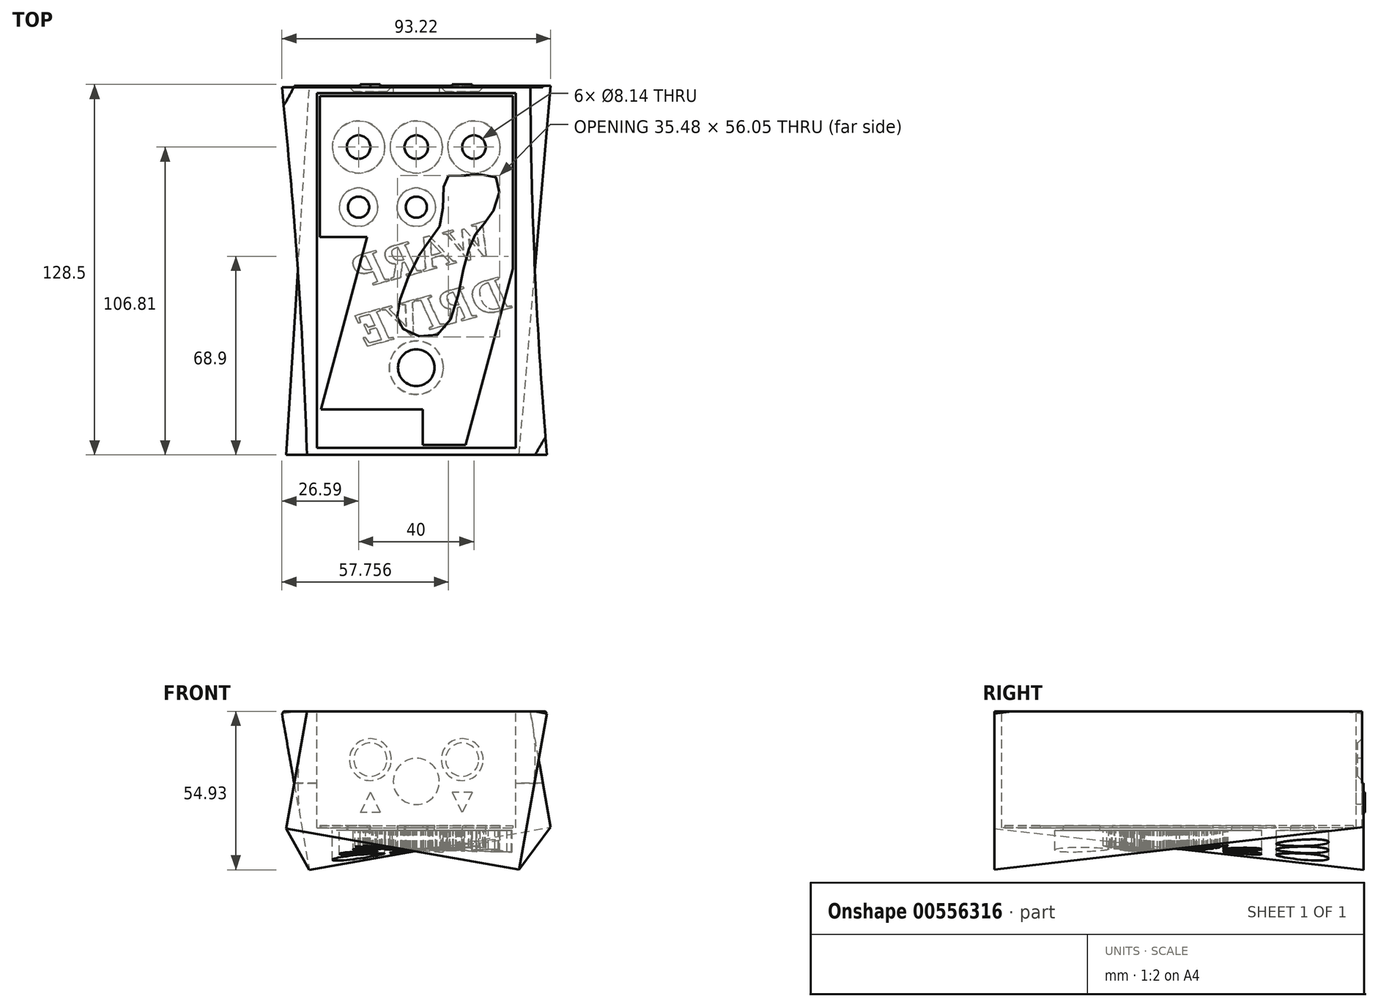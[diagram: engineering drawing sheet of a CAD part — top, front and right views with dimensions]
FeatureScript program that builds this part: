
annotation { "Feature Type Name" : "Feature", "Feature Type Description" : "" }
export const myFeature = defineFeature(function(context is Context, id is Id, definition is map)
    precondition{}
    {
        {
            var Q0;
            Q0=qCreatedBy(makeId("Top.planeOp"),FACE);
            var sketch = newSketch(context, id + "F0", { "sketchPlane" : qUnion([Q0])});
            skLineSegment(sketch, "E0.bottom", {"start": v(-36.5, 64) * mm, "end": v(36.5, 64) * mm});
            skLineSegment(sketch, "E0.top", {"start": v(-36.5, -64) * mm, "end": v(36.5, -64) * mm});
            skLineSegment(sketch, "E0.left", {"start": v(-36.5, 64) * mm, "end": v(-36.5, -64) * mm});
            skLineSegment(sketch, "E0.right", {"start": v(36.5, 64) * mm, "end": v(36.5, -64) * mm});
            skSolve(sketch);
        }
        {
            var Q0;
            Q0=makeQuery(id+"F0.imprint","IMPRINT",FACE,{"disambiguationData":[TD([[makeQuery(id+"F0.imprint","IMPRINT",EDGE,{"derivedFrom":sQuery(id+"F0.wireOp",EDGE,"E0.bottom")}),-1.0]])]});
            extrude(context, id + "F1", {"entities" : qUnion([Q0]), "depth" : 41.2 * mm, "offsetDistance" : 25 * mm});
        }
        {
            var Q0;
            Q0=makeQuery(id+"F1.opExtrude","SWEPT_FACE",FACE,{"disambiguationData":[OSD([sQuery(id+"F0.wireOp",EDGE,"E0.top")])]});
            var sketch = newSketch(context, id + "F2", { "sketchPlane" : qUnion([Q0])});
            skLineSegment(sketch, "E1.0", {"start": v(-36.5, 41.2) * mm, "end": v(-36.5, 0) * mm, "construction": true});
            skLineSegment(sketch, "E2", {"start": v(-36.5, 20.6) * mm, "end": v(36.5, 20.6) * mm, "construction": true});
            skLineSegment(sketch, "E3.bottom", {"start": v(-35.52, 54.74) * mm, "end": v(45.24, 40.5) * mm});
            skLineSegment(sketch, "E3.top", {"start": v(-45.07, 0.57) * mm, "end": v(35.68, -13.67) * mm});
            skLineSegment(sketch, "E3.left", {"start": v(-35.52, 54.74) * mm, "end": v(-45.07, 0.57) * mm});
            skLineSegment(sketch, "E3.right", {"start": v(45.24, 40.5) * mm, "end": v(35.68, -13.67) * mm});
            skPoint(sketch, "E3.middle", {"position": v(0, 20.6) * mm});
            skSolve(sketch);
        }
        {
            var Q0;
            Q0=makeQuery(id+"F1.opExtrude","SWEPT_FACE",FACE,{"disambiguationData":[OSD([sQuery(id+"F0.wireOp",EDGE,"E0.bottom")])]});
            var sketch = newSketch(context, id + "F3", { "sketchPlane" : qUnion([Q0])});
            skLineSegment(sketch, "E4.bottom", {"start": v(46.63, 40.44) * mm, "end": v(-37.08, 55.2) * mm});
            skLineSegment(sketch, "E4.top", {"start": v(37.08, -13.73) * mm, "end": v(-46.63, 1.03) * mm});
            skLineSegment(sketch, "E4.left", {"start": v(46.63, 40.44) * mm, "end": v(37.08, -13.73) * mm});
            skLineSegment(sketch, "E4.right", {"start": v(-37.08, 55.2) * mm, "end": v(-46.63, 1.03) * mm});
            skPoint(sketch, "E4.middle", {"position": v(0, 20.73) * mm});
            skSolve(sketch);
        }
        {
            var Q1;
            Q1 = qSketchRegion(id + "F2", true);
            var Q2;
            Q2 = qSketchRegion(id + "F3", true);
            var Q3;
            Q3=sQuery(id+"F2.wireOp",VERTEX,"E3.bottom.end");
            var Q4;
            Q4=sQuery(id+"F3.wireOp",VERTEX,"E4.bottom.end");
            loft(context, id + "F4", {"operationType" : NewBodyOperationType.ADD, "sheetProfilesArray" : [{ "sheetProfileEntities" : qUnion([Q1]) }, { "sheetProfileEntities" : qUnion([Q2]) }], "matchConnections" : true, "connections" : [{ "connectionEntities" : qUnion([Q3, Q4]), "connectionEdgeQueries" : qUnion([]), "connectionEdgeParameters" : [] }]});
        }
        {
            var Q0;
            Q0=qCreatedBy(makeId("Top.planeOp"),FACE);
            cPlane(context, id + "F5", {"entities" : qUnion([Q0]), "cplaneType" : CPlaneType.OFFSET, "offset" : 41.2 * mm, "width" : 150 * mm, "height" : 150 * mm});
        }
        {
            var Q0;
            Q0=qCreatedBy(id+"F5.planeOp",FACE);
            var sketch = newSketch(context, id + "F6", { "sketchPlane" : qUnion([Q0])});
            skLineSegment(sketch, "E5.bottom", {"start": v(-34.5, 61.5) * mm, "end": v(34.5, 61.5) * mm});
            skLineSegment(sketch, "E5.top", {"start": v(-34.5, -61.5) * mm, "end": v(34.5, -61.5) * mm});
            skLineSegment(sketch, "E5.left", {"start": v(-34.5, 61.5) * mm, "end": v(-34.5, -61.5) * mm});
            skLineSegment(sketch, "E5.right", {"start": v(34.5, 61.5) * mm, "end": v(34.5, -61.5) * mm});
            skSolve(sketch);
        }
        {
            var Q0;
            Q0=makeQuery(id+"F6.imprint","IMPRINT",FACE,{"disambiguationData":[TD([[makeQuery(id+"F6.imprint","IMPRINT",EDGE,{"derivedFrom":sQuery(id+"F6.wireOp",EDGE,"E5.bottom")}),-1.0]])]});
            extrude(context, id + "F7", {"entities" : qUnion([Q0]), "operationType" : NewBodyOperationType.REMOVE, "oppositeDirection" : true, "depth" : 40.4 * mm, "offsetDistance" : 25 * mm, "hasSecondDirection" : true, "secondDirectionOppositeDirection" : false, "secondDirectionDepth" : 25 * mm});
        }
        {
            var Q0;
            Q0=makeQuery(id+"F7.boolean.opBoolean","COPY",FACE,{"derivedFrom":makeQuery(id+"F7.opExtrude","CAP_FACE",FACE,{"disambiguationData":[OSD([sQuery(id+"F6.wireOp",EDGE,"E5.bottom"),sQuery(id+"F6.wireOp",EDGE,"E5.top"),sQuery(id+"F6.wireOp",EDGE,"E5.left"),sQuery(id+"F6.wireOp",EDGE,"E5.right")])],"isStart":false})});
            var sketch = newSketch(context, id + "F8", { "sketchPlane" : qUnion([Q0])});
            skCircle(sketch, "E6", {"center": v(-20, 42.8) * mm, "radius": 4.07 * mm});
            skCircle(sketch, "E7", {"center": v(0, 42.8) * mm, "radius": 4.07 * mm});
            skCircle(sketch, "E8", {"center": v(20, 42.8) * mm, "radius": 4.07 * mm});
            skCircle(sketch, "E9", {"center": v(0, -33.73) * mm, "radius": 6.35 * mm});
            skLineSegment(sketch, "E10", {"start": v(20, 42.8) * mm, "end": v(0, 42.8) * mm, "construction": true});
            skCircle(sketch, "E11", {"center": v(0, 21.96) * mm, "radius": 3.67 * mm});
            skCircle(sketch, "E12", {"center": v(-20, 21.96) * mm, "radius": 3.67 * mm});
            skSolve(sketch);
        }
        {
            var Q0;
            Q0=qSketchRegion(id+"F8",true);
            extrude(context, id + "F9", {"entities" : qUnion([Q0]), "operationType" : NewBodyOperationType.REMOVE, "oppositeDirection" : true, "depth" : 25 * mm, "offsetDistance" : 25 * mm});
        }
        {
            var Q0;
            Q0=makeQuery(id+"F7.boolean.opBoolean","COPY",FACE,{"derivedFrom":makeQuery(id+"F7.opExtrude","SWEPT_FACE",FACE,{"disambiguationData":[OSD([sQuery(id+"F6.wireOp",EDGE,"E5.bottom")])]})});
            cPlane(context, id + "F10", {"entities" : qUnion([Q0]), "cplaneType" : CPlaneType.OFFSET, "offset" : 2 * mm, "oppositeDirection" : true, "width" : 150 * mm, "height" : 150 * mm});
        }
        {
            var Q0;
            Q0=qCreatedBy(id+"F10.planeOp",FACE);
            var sketch = newSketch(context, id + "F11", { "sketchPlane" : qUnion([Q0])});
            skCircle(sketch, "E13", {"center": v(0, 16.93) * mm, "radius": 8 * mm});
            skCircle(sketch, "E14", {"center": v(15.92, 24.5) * mm, "radius": 5.76 * mm});
            skCircle(sketch, "E15", {"center": v(-15.92, 24.5) * mm, "radius": 5.76 * mm});
            skSolve(sketch);
        }
        {
            var Q0;
            Q0=qSketchRegion(id+"F11",true);
            extrude(context, id + "F12", {"entities" : qUnion([Q0]), "operationType" : NewBodyOperationType.REMOVE, "endBound" : BoundingType.SYMMETRIC, "oppositeDirection" : true, "depth" : 30 * mm, "offsetDistance" : 25 * mm});
        }
        {
            var Q0;
            Q0=qCreatedBy(id+"F10.planeOp",FACE);
            var sketch = newSketch(context, id + "F13", { "sketchPlane" : qUnion([Q0])});
            skLineSegment(sketch, "E16.0", {"start": v(-34.5, 0.8) * mm, "end": v(-34.5, 43) * mm});
            skLineSegment(sketch, "E17.0", {"start": v(-34.5, 0.8) * mm, "end": v(34.5, 0.8) * mm});
            skLineSegment(sketch, "E18.0", {"start": v(34.5, 0.8) * mm, "end": v(34.5, 43) * mm});
            skLineSegment(sketch, "E19.0", {"start": v(-34.5, 43) * mm, "end": v(34.5, 43) * mm});
            skSolve(sketch);
        }
        {
            var Q0;
            Q0=qSketchRegion(id+"F13",true);
            extrude(context, id + "F14", {"entities" : qUnion([Q0]), "operationType" : NewBodyOperationType.REMOVE, "oppositeDirection" : true, "depth" : 25 * mm, "offsetDistance" : 25 * mm});
        }
        {
            var Q0;
            Q0=makeQuery(id+"F14.boolean.opBoolean","COPY",FACE,{"derivedFrom":makeQuery(id+"F14.opExtrude","CAP_FACE",FACE,{"disambiguationData":[OSD([sQuery(id+"F13.wireOp",EDGE,"E16.0"),sQuery(id+"F13.wireOp",EDGE,"E17.0"),sQuery(id+"F13.wireOp",EDGE,"E18.0"),sQuery(id+"F13.wireOp",EDGE,"E19.0")])],"isStart":true})});
            var sketch = newSketch(context, id + "F15", { "sketchPlane" : qUnion([Q0])});
            skLineSegment(sketch, "E20", {"start": v(75, 16.26) * mm, "end": v(-75, 16.26) * mm});
            skLineSegment(sketch, "E21", {"start": v(-75, 16.26) * mm, "end": v(-75, 44.5) * mm});
            skLineSegment(sketch, "E22", {"start": v(-75, 44.5) * mm, "end": v(75, 44.5) * mm});
            skLineSegment(sketch, "E23", {"start": v(75, 44.5) * mm, "end": v(75, 16.26) * mm});
            skSolve(sketch);
        }
        {
            var Q0;
            Q0=qSketchRegion(id+"F15",true);
            extrude(context, id + "F16", {"entities" : qUnion([Q0]), "operationType" : NewBodyOperationType.REMOVE, "depth" : 15 * mm, "offsetDistance" : 25 * mm});
        }
        {
            var Q0;
            Q0=makeQuery(id+"F14.boolean.opBoolean","INTERSECT",EDGE,{"derivedFrom":[makeQuery(id+"F12.boolean.opBoolean","COPY",FACE,{"derivedFrom":makeQuery(id+"F12.opExtrude","SWEPT_FACE",FACE,{"disambiguationData":[OSD([sQuery(id+"F11.wireOp",EDGE,"E15")])]})}),makeQuery(id+"F14.opExtrude","CAP_FACE",FACE,{"disambiguationData":[OSD([sQuery(id+"F13.wireOp",EDGE,"E16.0"),sQuery(id+"F13.wireOp",EDGE,"E17.0"),sQuery(id+"F13.wireOp",EDGE,"E18.0"),sQuery(id+"F13.wireOp",EDGE,"E19.0")])],"isStart":true})]});
            var Q1;
            Q1=makeQuery(id+"F14.boolean.opBoolean","INTERSECT",EDGE,{"derivedFrom":[makeQuery(id+"F12.boolean.opBoolean","COPY",FACE,{"derivedFrom":makeQuery(id+"F12.opExtrude","SWEPT_FACE",FACE,{"disambiguationData":[OSD([sQuery(id+"F11.wireOp",EDGE,"E14")])]})}),makeQuery(id+"F14.opExtrude","CAP_FACE",FACE,{"disambiguationData":[OSD([sQuery(id+"F13.wireOp",EDGE,"E16.0"),sQuery(id+"F13.wireOp",EDGE,"E17.0"),sQuery(id+"F13.wireOp",EDGE,"E18.0"),sQuery(id+"F13.wireOp",EDGE,"E19.0")])],"isStart":true})]});
            chamfer(context, id + "F17", {"entities" : qUnion([Q0, Q1]), "width" : 1.5 * mm, "tangentPropagation" : true});
        }
        {
            var Q0;
            Q0=makeQuery(id+"F16.boolean.opBoolean","MERGE",FACE,{"derivedFrom":[makeQuery(id+"F14.boolean.opBoolean","COPY",FACE,{"derivedFrom":makeQuery(id+"F14.opExtrude","CAP_FACE",FACE,{"disambiguationData":[OSD([sQuery(id+"F13.wireOp",EDGE,"E16.0"),sQuery(id+"F13.wireOp",EDGE,"E17.0"),sQuery(id+"F13.wireOp",EDGE,"E18.0"),sQuery(id+"F13.wireOp",EDGE,"E19.0")])],"isStart":true})}),makeQuery(id+"F16.opExtrude","CAP_FACE",FACE,{"disambiguationData":[OSD([sQuery(id+"F15.wireOp",EDGE,"E20"),sQuery(id+"F15.wireOp",EDGE,"E21"),sQuery(id+"F15.wireOp",EDGE,"E22"),sQuery(id+"F15.wireOp",EDGE,"E23")])],"isStart":true})]});
            var sketch = newSketch(context, id + "F18", { "sketchPlane" : qUnion([Q0])});
            skLineSegment(sketch, "E24", {"start": v(15.92, 24.5) * mm, "end": v(15.92, 6.07) * mm, "construction": true});
            skLineSegment(sketch, "E25", {"start": v(-15.92, 24.5) * mm, "end": v(-15.92, 6.07) * mm, "construction": true});
            skLineSegment(sketch, "E26", {"start": v(-19.42, 13.12) * mm, "end": v(-15.92, 13.12) * mm});
            skLineSegment(sketch, "E27", {"start": v(-19.42, 13.12) * mm, "end": v(-15.92, 6.12) * mm});
            skLineSegment(sketch, "E28", {"start": v(15.92, 13.12) * mm, "end": v(19.42, 6.12) * mm});
            skLineSegment(sketch, "E29", {"start": v(19.42, 6.12) * mm, "end": v(15.92, 6.12) * mm});
            skLineSegment(sketch, "E30.MirrorCS", {"start": v(12.42, 6.12) * mm, "end": v(15.92, 6.12) * mm});
            skLineSegment(sketch, "E31.MirrorCS", {"start": v(15.92, 13.12) * mm, "end": v(12.42, 6.12) * mm});
            skLineSegment(sketch, "E32.MirrorCS", {"start": v(-12.42, 13.12) * mm, "end": v(-15.92, 6.12) * mm});
            skLineSegment(sketch, "E33.MirrorCS", {"start": v(-12.42, 13.12) * mm, "end": v(-15.92, 13.12) * mm});
            skSolve(sketch);
        }
        {
            var Q0;
            Q0=qSketchRegion(id+"F18",true);
            extrude(context, id + "F19", {"entities" : qUnion([Q0]), "operationType" : NewBodyOperationType.ADD, "depth" : 1 * mm, "offsetDistance" : 25 * mm});
        }
        {
            var Q0;
            {var subQ0=sQuery(id+"F6.wireOp",EDGE,"E5.bottom");var subQ1=sQuery(id+"F6.wireOp",EDGE,"E5.left");var subQ2=sQuery(id+"F6.wireOp",EDGE,"E5.top");var subQ3=sQuery(id+"F6.wireOp",EDGE,"E5.right");Q0=makeQuery(id+"FWr3AL7p3hajMNo_1.boolean.opBoolean","SPLIT",FACE,{"disambiguationData":[TD([makeQuery(id+"F7.boolean.opBoolean","COPY",FACE,{"derivedFrom":makeQuery(id+"F7.opExtrude","SWEPT_FACE",FACE,{"disambiguationData":[OSD([subQ0])]})})])],"derivedFrom":makeQuery(id+"F7.boolean.opBoolean","COPY",FACE,{"derivedFrom":makeQuery(id+"F7.opExtrude","CAP_FACE",FACE,{"disambiguationData":[OSD([subQ0,subQ2,subQ1,subQ3])],"isStart":false})})});}
            var sketch = newSketch(context, id + "F20", { "sketchPlane" : qUnion([Q0])});
            skLineSegment(sketch, "E34.bottom", {"start": v(-33.5, 60.5) * mm, "end": v(33.5, 60.5) * mm});
            skLineSegment(sketch, "E34.top", {"start": v(2.3, -60.5) * mm, "end": v(17.13, -60.5) * mm});
            skLineSegment(sketch, "E34.left", {"start": v(-33.5, 60.5) * mm, "end": v(-33.5, 11.66) * mm});
            skLineSegment(sketch, "E34.right", {"start": v(33.5, 60.5) * mm, "end": v(33.5, 0.6) * mm});
            skPoint(sketch, "E34.middle", {"position": v(0, 0) * mm});
            skCircle(sketch, "E35.0", {"center": v(-20, 42.8) * mm, "radius": 4.07 * mm});
            skCircle(sketch, "E36.0", {"center": v(0, 42.8) * mm, "radius": 4.07 * mm});
            skCircle(sketch, "E37.0", {"center": v(20, 42.8) * mm, "radius": 4.07 * mm});
            skCircle(sketch, "E38.0", {"center": v(0, 21.96) * mm, "radius": 3.67 * mm});
            skCircle(sketch, "E39.0", {"center": v(-20, 21.96) * mm, "radius": 3.68 * mm});
            skCircle(sketch, "E40.0", {"center": v(0, -33.73) * mm, "radius": 6.35 * mm});
            skFitSpline(sketch, "E41", {"points": [v(15.6, 32.92) * mm, v(10.24, 32.07) * mm, v(8.74, 17.26) * mm, v(3.16, 8.67) * mm, v(-6.28, -12.57) * mm, v(-4.57, -20.3) * mm, v(7.88, -22.02) * mm, v(16.25, 0) * mm, v(20.97, 13.18) * mm, v(26.55, 20.26) * mm, v(27.84, 32.07) * mm, v(15.6, 32.92) * mm]});
            skLineSegment(sketch, "E42", {"start": v(-33.1, -48.2) * mm, "end": v(-17.05, 11.66) * mm});
            skLineSegment(sketch, "E43", {"start": v(-17.05, 11.66) * mm, "end": v(-33.5, 11.66) * mm});
            skLineSegment(sketch, "E44", {"start": v(-33.1, -48.2) * mm, "end": v(2.3, -48.2) * mm});
            skLineSegment(sketch, "E45", {"start": v(2.3, -48.2) * mm, "end": v(2.3, -60.5) * mm});
            skPoint(sketch, "E46.orphan", {"position": v(-33.5, -60.5) * mm});
            skLineSegment(sketch, "E47", {"start": v(17.13, -60.5) * mm, "end": v(33.5, 0.6) * mm});
            skPoint(sketch, "E48.orphan", {"position": v(33.5, -60.5) * mm});
            skSolve(sketch);
        }
        {
            var Q0;
            Q0=qSketchRegion(id+"F20",true);
            extrude(context, id + "F21", {"entities" : qUnion([Q0]), "depth" : 0.8 * mm, "offsetDistance" : 25 * mm});
        }
        {
            var Q0;
            Q0=qCreatedBy(makeId("Top.planeOp"),FACE);
            var sketch = newSketch(context, id + "F22", { "sketchPlane" : qUnion([Q0])});
            skCircle(sketch, "E49.0", {"center": v(0, -33.73) * mm, "radius": 6.35 * mm, "construction": true});
            skCircle(sketch, "E50.0", {"center": v(0, 21.96) * mm, "radius": 3.67 * mm, "construction": true});
            skCircle(sketch, "E51.0", {"center": v(20, 42.8) * mm, "radius": 4.07 * mm, "construction": true});
            skCircle(sketch, "E52.0", {"center": v(0, 42.8) * mm, "radius": 4.07 * mm, "construction": true});
            skCircle(sketch, "E53.0", {"center": v(-20, 21.96) * mm, "radius": 3.68 * mm, "construction": true});
            skCircle(sketch, "E54.0", {"center": v(-20, 42.8) * mm, "radius": 4.07 * mm, "construction": true});
            skCircle(sketch, "E55", {"center": v(0, -33.73) * mm, "radius": 9.35 * mm});
            skCircle(sketch, "E56", {"center": v(0, 21.96) * mm, "radius": 6.68 * mm});
            skCircle(sketch, "E57", {"center": v(20, 42.8) * mm, "radius": 9.07 * mm});
            skCircle(sketch, "E58", {"center": v(0, 42.8) * mm, "radius": 9.07 * mm});
            skCircle(sketch, "E59", {"center": v(-20, 21.96) * mm, "radius": 6.68 * mm});
            skCircle(sketch, "E60", {"center": v(-20, 42.8) * mm, "radius": 9.07 * mm});
            skSolve(sketch);
        }
        {
            var Q0;
            Q0 = qSketchRegion(id + "F22", true);
            extrude(context, id + "F23", {"entities" : qUnion([Q0]), "operationType" : NewBodyOperationType.REMOVE, "oppositeDirection" : true, "depth" : 25 * mm, "offsetDistance" : 25 * mm});
        }
        {
            var Q0;
            Q0=qCreatedBy(id+"F5.planeOp",FACE);
            var sketch = newSketch(context, id + "F24", { "sketchPlane" : qUnion([Q0])});
            skLineSegment(sketch, "E61.bottom", {"start": v(61.89, -73.5) * mm, "end": v(-61.89, -73.5) * mm});
            skLineSegment(sketch, "E61.top", {"start": v(61.89, 73.5) * mm, "end": v(-61.89, 73.5) * mm});
            skLineSegment(sketch, "E61.left", {"start": v(61.89, -73.5) * mm, "end": v(61.89, 73.5) * mm});
            skLineSegment(sketch, "E61.right", {"start": v(-61.89, -73.5) * mm, "end": v(-61.89, 73.5) * mm});
            skPoint(sketch, "E61.middle", {"position": v(0, 0) * mm});
            skSolve(sketch);
        }
        {
            var Q0;
            Q0 = qSketchRegion(id + "F24", true);
            extrude(context, id + "F25", {"entities" : qUnion([Q0]), "operationType" : NewBodyOperationType.REMOVE, "depth" : 25 * mm, "offsetDistance" : 25 * mm});
        }
        {
            var Q0;
            Q0=makeQuery(id+"F23.boolean.opBoolean","COPY",FACE,{"derivedFrom":makeQuery(id+"F23.opExtrude","CAP_FACE",FACE,{"disambiguationData":[OSD([sQuery(id+"F22.wireOp",EDGE,"E57")])],"isStart":true})});
            var sketch = newSketch(context, id + "F26", { "sketchPlane" : qUnion([Q0])});
            skText(sketch, "E62", { "text": "WARP\nDRIVE", "fontName": "Tinos-BoldItalic.ttf"});
            const initialGuessF26  = {"E62": [0.02794, -0.00638, -0.96627, 0.25753, 0.0125]};
            skSetInitialGuess(sketch, initialGuessF26);
            skSolve(sketch);
        }
        {
            var Q0;
            Q0 = qSketchRegion(id + "F26", true);
            extrude(context, id + "F27", {"entities" : qUnion([Q0]), "operationType" : NewBodyOperationType.REMOVE, "depth" : 25 * mm, "offsetDistance" : 25 * mm});
        }
    });
